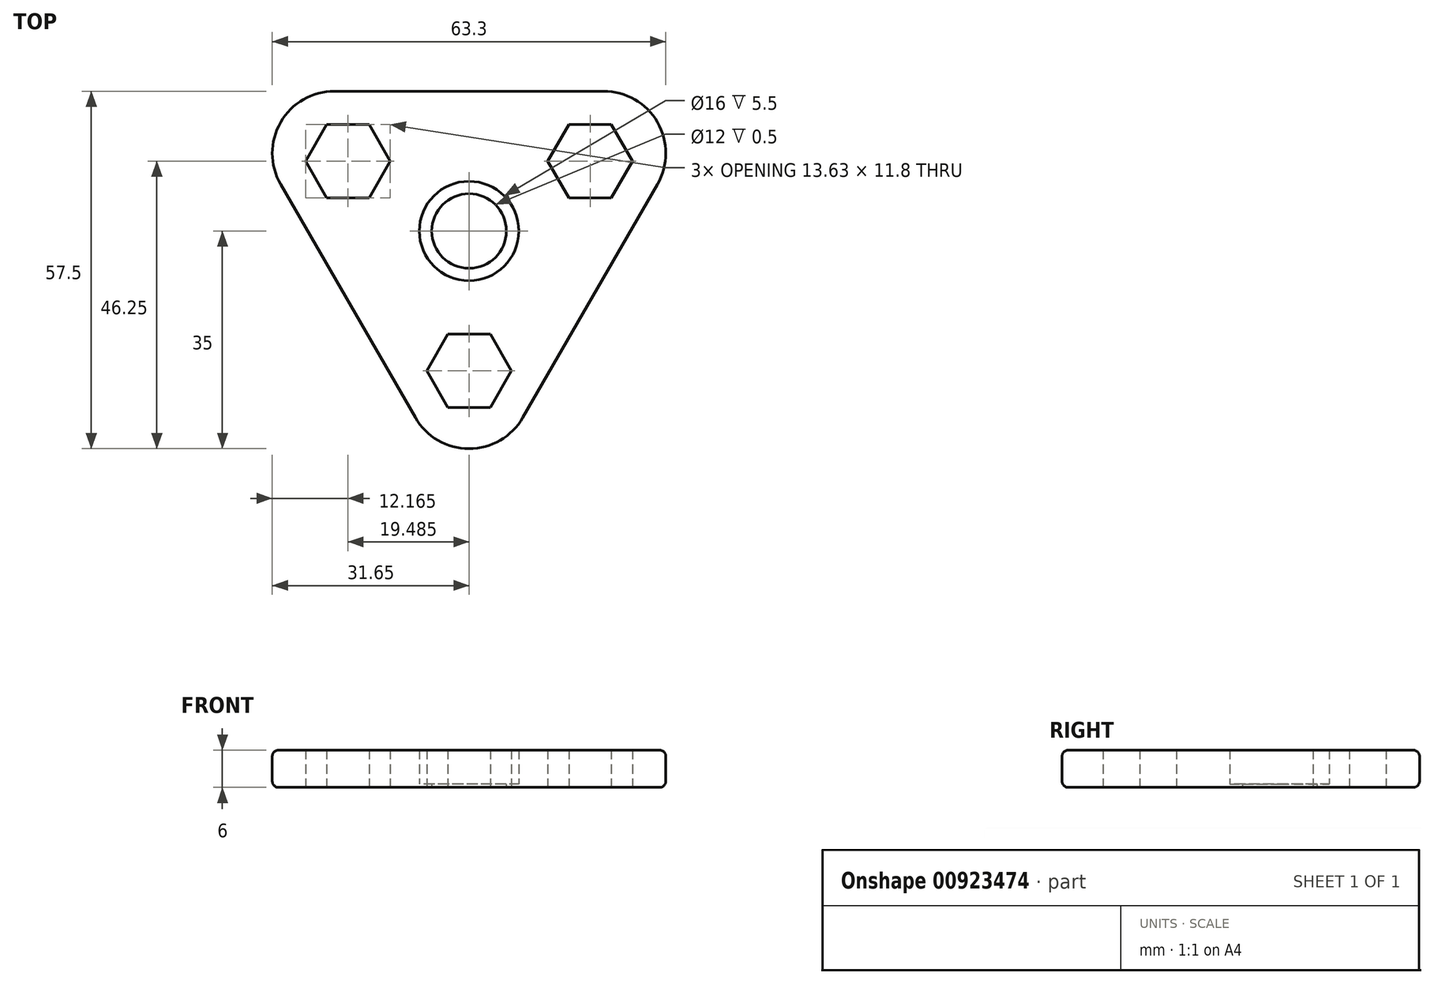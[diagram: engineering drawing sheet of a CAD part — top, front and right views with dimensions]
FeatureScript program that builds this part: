
annotation { "Feature Type Name" : "Feature", "Feature Type Description" : "" }
export const myFeature = defineFeature(function(context is Context, id is Id, definition is map)
    precondition{}
    {
        {
            var Q0;
            Q0=qCreatedBy(makeId("Top.planeOp"),FACE);
            var sketch = newSketch(context, id + "F0", { "sketchPlane" : qUnion([Q0])});
            skCircle(sketch, "E0", {"center": v(0, 0) * mm, "radius": 8 * mm});
            skCircle(sketch, "E1.cCircle", {"center": v(0, 0) * mm, "radius": 22.5 * mm, "construction": true});
            skLineSegment(sketch, "E1.0", {"start": v(30.31, 7.5) * mm, "end": v(8.66, -30) * mm});
            skLineSegment(sketch, "E1.1", {"start": v(-8.66, -30) * mm, "end": v(-30.31, 7.5) * mm});
            skLineSegment(sketch, "E1.2", {"start": v(-21.65, 22.5) * mm, "end": v(21.65, 22.5) * mm});
            skPoint(sketch, "E1.0.midPoint", {"position": v(19.49, -11.25) * mm});
            skLineSegment(sketch, "E2", {"start": v(-38.97, 22.5) * mm, "end": v(19.49, -11.25) * mm, "construction": true});
            skLineSegment(sketch, "E3", {"start": v(38.97, 22.5) * mm, "end": v(-19.49, -11.25) * mm, "construction": true});
            skLineSegment(sketch, "E4", {"start": v(0, 22.5) * mm, "end": v(0, -45) * mm, "construction": true});
            skPoint(sketch, "E5.visualSharp", {"position": v(-38.97, 22.5) * mm});
            skArc(sketch, "E5.filletArc", {"start": v(-21.65, 22.5) * mm, "mid": v(-30.31, 17.5) * mm, "end": v(-30.31, 7.5) * mm});
            skPoint(sketch, "E6.visualSharp", {"position": v(38.97, 22.5) * mm});
            skArc(sketch, "E6.filletArc", {"start": v(30.31, 7.5) * mm, "mid": v(30.31, 17.5) * mm, "end": v(21.65, 22.5) * mm});
            skPoint(sketch, "E7.visualSharp", {"position": v(0, -45) * mm});
            skArc(sketch, "E7.filletArc", {"start": v(-8.66, -30) * mm, "mid": v(0, -35) * mm, "end": v(8.66, -30) * mm});
            skCircle(sketch, "E8.cCircle", {"center": v(-19.49, 11.25) * mm, "radius": 5.9 * mm, "construction": true});
            skLineSegment(sketch, "E8.0", {"start": v(-12.67, 11.25) * mm, "end": v(-16.08, 5.35) * mm});
            skLineSegment(sketch, "E8.1", {"start": v(-16.08, 5.35) * mm, "end": v(-22.9, 5.35) * mm});
            skLineSegment(sketch, "E8.2", {"start": v(-22.9, 5.35) * mm, "end": v(-26.3, 11.25) * mm});
            skLineSegment(sketch, "E8.3", {"start": v(-26.3, 11.25) * mm, "end": v(-22.9, 17.15) * mm});
            skLineSegment(sketch, "E8.4", {"start": v(-22.9, 17.15) * mm, "end": v(-16.08, 17.15) * mm});
            skLineSegment(sketch, "E8.5", {"start": v(-16.08, 17.15) * mm, "end": v(-12.67, 11.25) * mm});
            skPoint(sketch, "E8.0.midPoint", {"position": v(-14.38, 8.3) * mm});
            skCircle(sketch, "E9.cCircle", {"center": v(19.49, 11.25) * mm, "radius": 5.9 * mm, "construction": true});
            skLineSegment(sketch, "E9.0", {"start": v(16.08, 5.35) * mm, "end": v(12.67, 11.25) * mm});
            skLineSegment(sketch, "E9.1", {"start": v(12.67, 11.25) * mm, "end": v(16.08, 17.15) * mm});
            skLineSegment(sketch, "E9.2", {"start": v(16.08, 17.15) * mm, "end": v(22.9, 17.15) * mm});
            skLineSegment(sketch, "E9.3", {"start": v(22.9, 17.15) * mm, "end": v(26.3, 11.25) * mm});
            skLineSegment(sketch, "E9.4", {"start": v(26.3, 11.25) * mm, "end": v(22.9, 5.35) * mm});
            skLineSegment(sketch, "E9.5", {"start": v(22.9, 5.35) * mm, "end": v(16.08, 5.35) * mm});
            skPoint(sketch, "E9.0.midPoint", {"position": v(14.38, 8.3) * mm});
            skCircle(sketch, "E10.cCircle", {"center": v(0, -22.5) * mm, "radius": 5.9 * mm, "construction": true});
            skLineSegment(sketch, "E10.0", {"start": v(3.4, -16.6) * mm, "end": v(6.81, -22.5) * mm});
            skLineSegment(sketch, "E10.1", {"start": v(6.81, -22.5) * mm, "end": v(3.4, -28.4) * mm});
            skLineSegment(sketch, "E10.2", {"start": v(3.4, -28.4) * mm, "end": v(-3.4, -28.4) * mm});
            skLineSegment(sketch, "E10.3", {"start": v(-3.4, -28.4) * mm, "end": v(-6.81, -22.5) * mm});
            skLineSegment(sketch, "E10.4", {"start": v(-6.81, -22.5) * mm, "end": v(-3.4, -16.6) * mm});
            skLineSegment(sketch, "E10.5", {"start": v(-3.4, -16.6) * mm, "end": v(3.4, -16.6) * mm});
            skPoint(sketch, "E10.0.midPoint", {"position": v(5.1, -19.55) * mm});
            skSolve(sketch);
        }
        {
            var Q0;
            Q0 = qSketchRegion(id + "F0", true);
            extrude(context, id + "F1", {"entities" : qUnion([Q0]), "depth" : 6 * mm, "offsetDistance" : 25 * mm});
        }
        {
            var Q0;
            Q0=qCreatedBy(makeId("Top.planeOp"),FACE);
            var sketch = newSketch(context, id + "F2", { "sketchPlane" : qUnion([Q0])});
            skCircle(sketch, "E11", {"center": v(0, 0) * mm, "radius": 6 * mm});
            skCircle(sketch, "E12", {"center": v(0, 0) * mm, "radius": 8 * mm});
            skSolve(sketch);
        }
        {
            var Q0;
            Q0 = qSketchRegion(id + "F2", true);
            extrude(context, id + "F3", {"entities" : qUnion([Q0]), "operationType" : NewBodyOperationType.ADD, "depth" : 0.5 * mm, "offsetDistance" : 25 * mm});
        }
        {
            var Q0;
            Q0=makeQuery(id+"F1.opExtrude","CAP_EDGE",EDGE,{"disambiguationData":[OSD([sQuery(id+"F0.wireOp",EDGE,"E1.2")])],"isStart":false});
            var Q1;
            Q1=makeQuery(id+"F1.opExtrude","CAP_EDGE",EDGE,{"disambiguationData":[OSD([sQuery(id+"F0.wireOp",EDGE,"E1.2")])],"isStart":true});
            fillet(context, id + "F4", {"entities" : qUnion([Q0, Q1]), "radius" : 1 * mm, "tangentPropagation" : true, "allowEdgeOverflow" : false});
        }
    });
